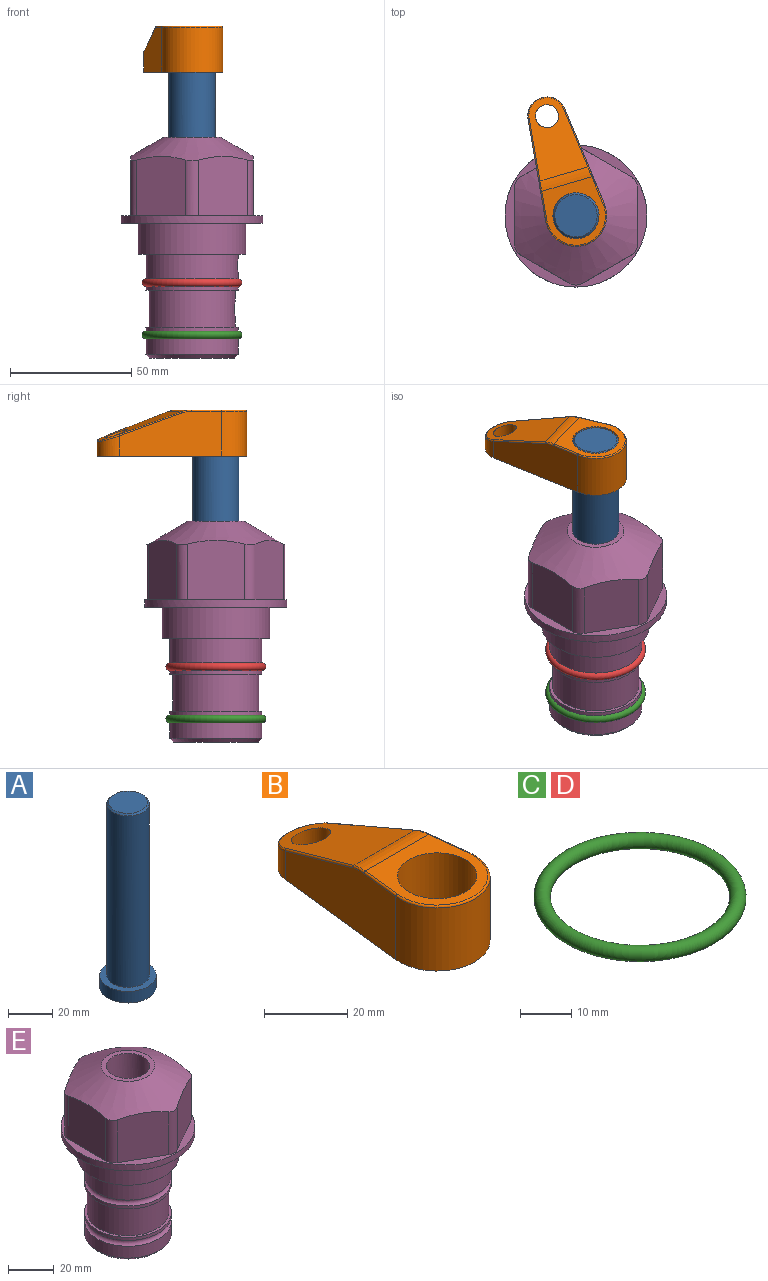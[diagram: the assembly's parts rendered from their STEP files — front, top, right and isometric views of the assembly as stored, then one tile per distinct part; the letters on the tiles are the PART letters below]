
ASSEMBLY  parts=5 mates=3
PART A: 6 faces, bbox 25.4x25.4x101.6 mm
  f0: plane 17.46x17.46mm, normal (0,0,1), area 239.5mm2, adj f5
  f1: plane 25.4x25.4mm, normal (0,0,-1), area 506.7mm2, adj f2
  f2: cylinder r=12.7mm len=25.4mm, axis (0,0,1), area 506.7mm2, adj f1,f3
  f3: plane 25.4x25.4mm, normal (0,0,1), area 221.7mm2, adj f2,f4
  f4: cylinder r=9.53mm len=94.46mm, axis (0,0,1), area 5653mm2, adj f3,f5
  f5: cone r=8.73mm half-angle=45deg, axis (0,0,-1), area 64.4mm2, adj f0,f4
PART B: 44 faces, bbox 27.5x64.5x19.1 mm
  f0: plane 2.3x0.95mm, normal (0,0,-1), area 1mm2, adj f25,f30,f34
  f1: plane 63.5x25.4mm, normal (0,0,-1), area 561.7mm2, adj f2,f3,f4,f5,f6,f7,f19,f20
  f2: cylinder r=12.7mm len=25.4mm, axis (0,0,-1), area 792.2mm2, adj f1,f3,f5,f13
  f3: plane 42.33x18.54mm, normal (0.99,0.11,0), area 647mm2, adj f1,f2,f4,f11,f12,f14
  f4: cylinder r=7.94mm len=15.78mm, axis (0,0,-1), area 158.6mm2, adj f1,f3,f5,f16
  f5: plane 42.33x18.54mm, normal (-0.99,0.11,0), area 647mm2, adj f1,f2,f4,f15,f17,f18
  f6: cylinder r=9.53mm len=19.05mm, axis (0,0,-1), area 1140.1mm2, adj f1,f8
  f7: cylinder r=4.76mm len=10.98mm, axis (0,0,-1), area 276.1mm2, adj f1,f9
  f8: plane 25.83x24.38mm, normal (0,0,1), area 262.2mm2, adj f6,f10,f11,f13,f15
  f9: plane 32.49x20.55mm, normal (0,0.34,0.94), area 489.9mm2, adj f7,f10,f14,f16,f18
  f10: cylinder r=12.7mm len=21.49mm, axis (-1,0,0), area 93.2mm2, adj f8,f9,f12,f17
  f11: cylinder r=0.51mm len=12.34mm, axis (0.11,-0.99,0), area 9.9mm2, adj f3,f8,f12,f13
  f12: bspline ~7.62x1.64mm, area 3.5mm2, adj f3,f10,f11,f14
  f13: torus R=12.19mm, axis (0,0,1), area 33.6mm2, adj f2,f8,f11,f15
  f14: cylinder r=0.51mm len=26.01mm, axis (0.1,-0.93,0.34), area 21.6mm2, adj f3,f9,f12,f16
  f15: cylinder r=0.51mm len=12.34mm, axis (0.11,0.99,0), area 9.9mm2, adj f5,f8,f13,f17
  f16: bspline ~15.78x7.05mm, area 15.7mm2, adj f4,f9,f14,f18
  f17: bspline ~7.62x1.64mm, area 3.5mm2, adj f5,f10,f15,f18
  f18: cylinder r=0.51mm len=26.01mm, axis (0.1,0.93,-0.34), area 21.6mm2, adj f5,f9,f16,f17
  f19: plane 21.6x14.29mm, normal (-0.99,-0.11,0), area 242.6mm2, adj f1,f26,f28,f34,f36,f38
  f20: plane 21.6x14.29mm, normal (0.99,-0.11,0), area 242.6mm2, adj f1,f27,f29,f37,f39,f41
  f21: cylinder r=12.7mm len=14.29mm, axis (0,0,-1), area 173.2mm2, adj f1,f26,f27,f30,f31,f33
  f22: cylinder r=7.94mm len=7.63mm, axis (0,0,-1), area 53.8mm2, adj f1,f28,f29,f42
  f23: plane 2.3x0.95mm, normal (0,0,-1), area 1mm2, adj f25,f33,f37
  f24: plane 17.94x12.32mm, normal (0,-0.34,-0.94), area 191.2mm2, adj f25,f38,f41,f42
  f25: cylinder r=9.53mm len=12.93mm, axis (-1,0,0), area 37.5mm2, adj f0,f23,f24,f31,f36,f39
  f26: cylinder r=1.59mm len=14.29mm, axis (0,0,-1), area 49mm2, adj f1,f19,f21,f32
  f27: cylinder r=1.59mm len=14.29mm, axis (0,0,-1), area 49mm2, adj f1,f20,f21,f35
  f28: cylinder r=1.59mm len=7.28mm, axis (0,0,-1), area 22.1mm2, adj f1,f19,f22,f40
  f29: cylinder r=1.59mm len=7.28mm, axis (0,0,-1), area 22.1mm2, adj f1,f20,f22,f43
  f30: torus R=14.29mm, axis (0,0,1), area 5.8mm2, adj f0,f21,f31,f32
  f31: bspline ~11.06x2.73mm, area 20.8mm2, adj f21,f25,f30,f33
  f32: sphere r=1.59mm, area 5.4mm2, adj f26,f30,f34
  f33: torus R=14.29mm, axis (0,0,1), area 5.8mm2, adj f21,f23,f31,f35
  f34: cylinder r=1.59mm len=1.68mm, axis (-0.11,0.99,0), area 2.4mm2, adj f0,f19,f32,f36
  f35: sphere r=1.59mm, area 5.4mm2, adj f27,f33,f37
  f36: bspline ~5.82x2.33mm, area 7.7mm2, adj f19,f25,f34,f38
  f37: cylinder r=1.59mm len=1.68mm, axis (0.11,0.99,0), area 2.4mm2, adj f20,f23,f35,f39
  f38: cylinder r=1.59mm len=18.33mm, axis (0.1,-0.93,0.34), area 46.7mm2, adj f19,f24,f36,f40
  f39: bspline ~5.82x2.33mm, area 7.7mm2, adj f20,f25,f37,f41
  f40: sphere r=1.59mm, area 3.6mm2, adj f28,f38,f42
  f41: cylinder r=1.59mm len=18.33mm, axis (0.1,0.93,-0.34), area 46.7mm2, adj f20,f24,f39,f43
  f42: bspline ~8.31x1.84mm, area 15.3mm2, adj f22,f24,f40,f43
  f43: sphere r=1.59mm, area 3.6mm2, adj f29,f41,f42
PART C: 1 faces, bbox 44.7x44.7x3.2 mm
  f0: torus R=19.05mm, axis (0,0,1), area 1193.9mm2
PART D: same geometry as C
PART E: 36 faces, bbox 58.7x58.7x91.2 mm
  f0: cylinder r=17.78mm len=35.56mm, axis (0,0,1), area 1670.8mm2, adj f23,f24,f31
  f1: cylinder r=19.05mm len=38.1mm, axis (0,0,1), area 1191.9mm2, adj f26,f27,f30
  f2: plane 58.66x58.66mm, normal (0,0,-1), area 1150.6mm2, adj f3,f28
  f3: cylinder r=29.33mm len=58.66mm, axis (0,0,-1), area 585.1mm2, adj f2,f4
  f4: plane 58.66x58.66mm, normal (0,0,1), area 475.9mm2, adj f3,f5,f6,f7,f8,f9,f10,f11
  f5: plane 24.5x20.32mm, normal (-0.5,0.87,0), area 562.8mm2, adj f4,f15,f16,f17
  f6: plane 24.5x20.32mm, normal (0.5,0.87,0), area 562.8mm2, adj f4,f14,f15,f17
  f7: plane 24.5x23.48mm, normal (1,0,0), area 562.8mm2, adj f4,f13,f14,f17
  f8: plane 24.5x20.32mm, normal (0.5,-0.87,0), area 562.8mm2, adj f4,f12,f13,f17
  f9: plane 24.5x20.32mm, normal (-0.5,-0.87,0), area 562.8mm2, adj f4,f11,f12,f17
  f10: plane 24.5x23.48mm, normal (-1,0,0), area 562.8mm2, adj f4,f11,f16,f17
  f11: cylinder r=5.08mm len=23.01mm, axis (0,0,-1), area 121.2mm2, adj f4,f9,f10,f17
  f12: cylinder r=5.08mm len=23.01mm, axis (0,0,-1), area 121.2mm2, adj f4,f8,f9,f17
  f13: cylinder r=5.08mm len=23.01mm, axis (0,0,-1), area 121.2mm2, adj f4,f7,f8,f17
  f14: cylinder r=5.08mm len=23.01mm, axis (0,0,-1), area 121.2mm2, adj f4,f6,f7,f17
  f15: cylinder r=5.08mm len=23.01mm, axis (0,0,-1), area 121.2mm2, adj f4,f5,f6,f17
  f16: cylinder r=5.08mm len=23.01mm, axis (0,0,-1), area 121.2mm2, adj f4,f5,f10,f17
  f17: cone r=11.73mm half-angle=60deg, axis (0,0,-1), area 2071.8mm2, adj f5,f6,f7,f8,f9,f10,f11,f12
  f18: plane 23.46x23.46mm, normal (0,0,1), area 147.4mm2, adj f17,f35
  f19: plane 34.93x34.93mm, normal (0,0,-1), area 958mm2, adj f29
  f20: cylinder r=19.05mm len=38.1mm, axis (0,0,1), area 760.1mm2, adj f21,f29
  f21: torus R=19.05mm, axis (0,0,1), area 565.3mm2, adj f20,f22
  f22: cylinder r=19.05mm len=38.1mm, axis (0,0,1), area 190mm2, adj f21,f23
  f23: plane 38.1x38.1mm, normal (0,0,1), area 146.9mm2, adj f0,f22
  f24: plane 38.1x38.1mm, normal (0,0,-1), area 146.9mm2, adj f0,f25
  f25: cylinder r=19.05mm len=38.1mm, axis (0,0,1), area 190mm2, adj f24,f26
  f26: torus R=19.05mm, axis (0,0,1), area 565.3mm2, adj f1,f25
  f27: plane 44.45x44.45mm, normal (0,0,-1), area 411.7mm2, adj f1,f28
  f28: cylinder r=22.23mm len=44.45mm, axis (0,0,1), area 1773.5mm2, adj f2,f27
  f29: cone r=19.05mm half-angle=45deg, axis (0,0,1), area 257.5mm2, adj f19,f20
  f30: cylinder r=3.17mm len=6.75mm, axis (-1,0,0), area 128mm2, adj f1,f33
  f31: cylinder r=3.17mm len=6.35mm, axis (-1,0,0), area 102.5mm2, adj f0,f33
  f32: plane 25.4x25.4mm, normal (0,0,1), area 506.7mm2, adj f33
  f33: cylinder r=12.7mm len=66.42mm, axis (0,0,-1), area 5236.2mm2, adj f30,f31,f32,f34
  f34: cone r=9.53mm half-angle=30deg, axis (0,0,-1), area 443.4mm2, adj f33,f35
  f35: cylinder r=9.53mm len=19.05mm, axis (0,0,-1), area 849mm2, adj f18,f34
PLACE A rot(axis=(0,0,1),106.2deg) t=(0,0,7.89)mm
PLACE B rot(axis=(0,0,1),16.2deg) t=(0,0,62.5)mm
PLACE C t=(0,0,-21.59)mm
PLACE D at identity
PLACE E at identity fixed
MATE fastened C.f0 <-> E.f0  axis (0,0,1) through (0,0,-46.1)mm
MATE cylindrical A.f2 <-> E.f0  axis (0,0,1) through (0,0,33.53)mm
MATE fastened B.f2 <-> A.f2  axis (0,0,1) through (0,0,81.55)mm
